# Revit family: QSP1
name_source: partatom
category: Lighting Fixtures
revit_build: Autodesk Revit MEP 2012 (Build: 20110309_2315(x64)
units: mm (PartAtom-declared; Revit-internal decimal feet)

## types (5) — shared parameters
Apparent Load = 0 VA
Color Filter = 16777215
Default Elevation = 48"
Description = Architectural wallpack in two stylish shapes.
Dimming Lamp Color Temperature Shift = <None>
Emit Shape Visible in Rendering = No
Emit from Circle Diameter = 6"
Lamp = LED
Load Classification = Lighting
Manufacturer = Hubbell Outdoor
Manufacturer Fax = (864)-678-1065
Model = QSP1
Opal lens = Etched Glass
Photometric Link = http://www.hubbelloutdoor.com
Photometric Web File = RDI 42F WT TRP RTP QSP.ies
Product Documentation Link = http://cdn.hubbelloutdoor.com
Product Page URL = http://www.hubbelloutdoor.com
Tilt Angle = -90.00°
URL = http://www.hubbelloutdoor.com
Voltage = 120 V
Wattage Comments = 15W/20W/30W

## per-type parameters (varying)
| type | Finish |
| QSP PS | Platinum |
| QSP BK | Black |
| QSP GR | Gray |
| QSP WH | White |
| QSP DB | Bronze |

## geometry (parser evidence)
native form markers: Sweep x2
no freeform markers — native parametric forms only
